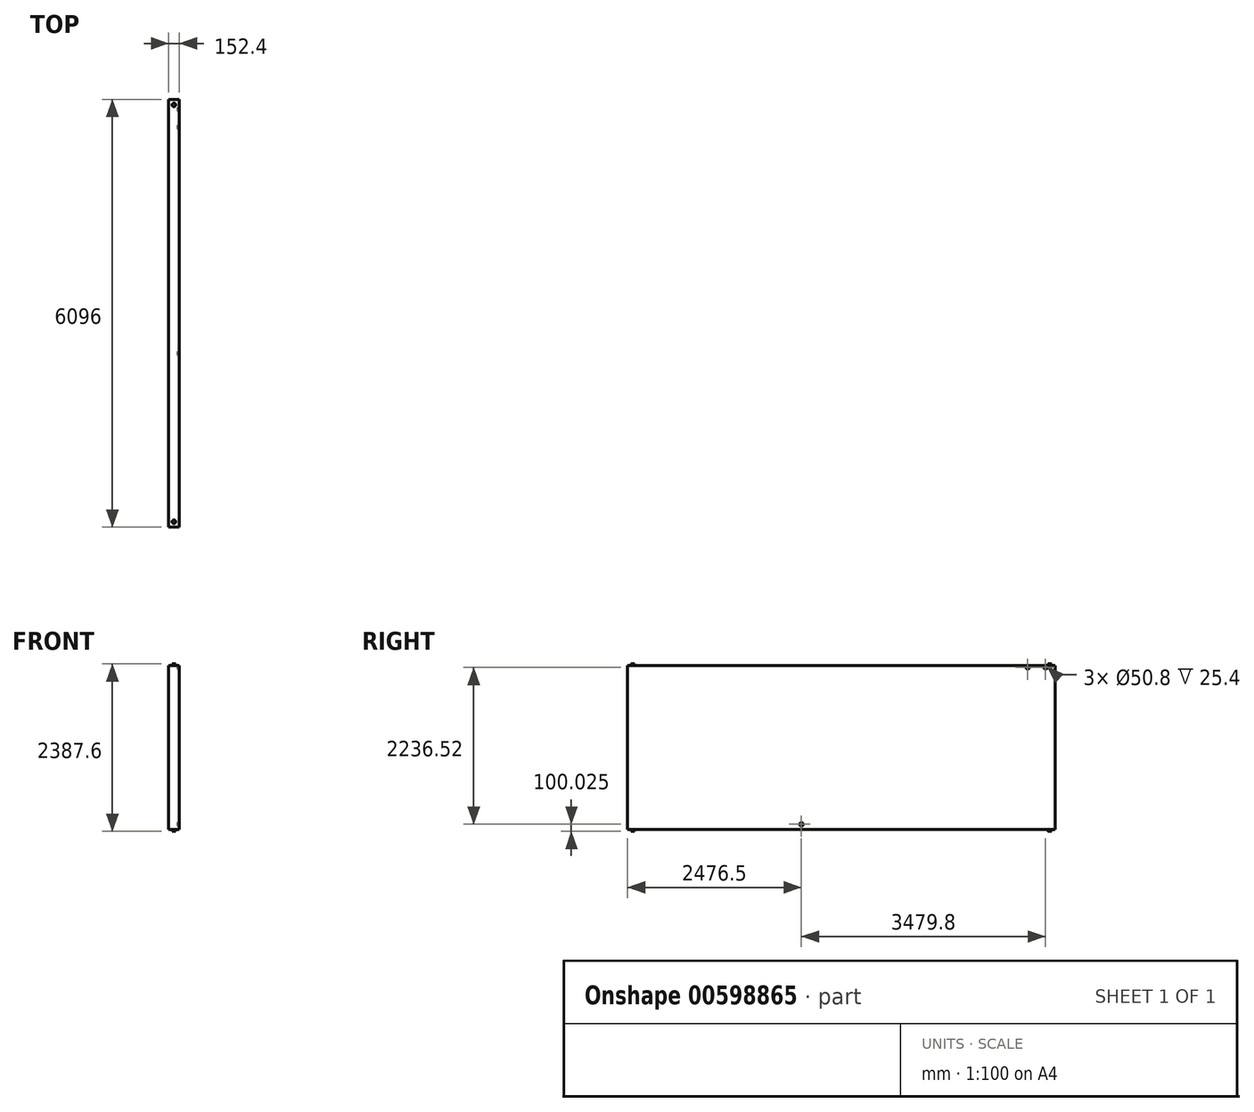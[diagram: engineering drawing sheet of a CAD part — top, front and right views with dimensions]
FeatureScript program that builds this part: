
annotation { "Feature Type Name" : "Feature", "Feature Type Description" : "" }
export const myFeature = defineFeature(function(context is Context, id is Id, definition is map)
    precondition{}
    {
        {
            var Q0;
            Q0=qCreatedBy(makeId("Top.planeOp"),FACE);
            var sketch = newSketch(context, id + "F0", { "sketchPlane" : qUnion([Q0])});
            skLineSegment(sketch, "E0.bottom", {"start": v(76.2, 3048) * mm, "end": v(-76.2, 3048) * mm});
            skLineSegment(sketch, "E0.top", {"start": v(76.2, -3048) * mm, "end": v(-76.2, -3048) * mm});
            skLineSegment(sketch, "E0.left", {"start": v(76.2, 3048) * mm, "end": v(76.2, -3048) * mm});
            skLineSegment(sketch, "E0.right", {"start": v(-76.2, 3048) * mm, "end": v(-76.2, -3048) * mm});
            skPoint(sketch, "E0.middle", {"position": v(0, 0) * mm});
            skSolve(sketch);
        }
        {
            var Q0;
            Q0=makeQuery(id+"F0.imprint","IMPRINT",FACE,{"disambiguationData":[TD([[makeQuery(id+"F0.imprint","IMPRINT",EDGE,{"derivedFrom":sQuery(id+"F0.wireOp",EDGE,"E0.bottom")}),1.0]])]});
            extrude(context, id + "F1", {"entities" : qUnion([Q0]), "depth" : 2336.8 * mm, "offsetDistance" : 25.4 * mm});
        }
        {
            var Q0;
            Q0=makeQuery(id+"F1.opExtrude","CAP_FACE",FACE,{"disambiguationData":[OSD([sQuery(id+"F0.wireOp",EDGE,"E0.bottom"),sQuery(id+"F0.wireOp",EDGE,"E0.top"),sQuery(id+"F0.wireOp",EDGE,"E0.left"),sQuery(id+"F0.wireOp",EDGE,"E0.right")])],"isStart":false});
            var sketch = newSketch(context, id + "F2", { "sketchPlane" : qUnion([Q0])});
            skLineSegment(sketch, "E1.bottom", {"start": v(76.2, -3048) * mm, "end": v(0, -3048) * mm});
            skLineSegment(sketch, "E1.top", {"start": v(76.2, -2971.8) * mm, "end": v(0, -2971.8) * mm});
            skLineSegment(sketch, "E1.left", {"start": v(76.2, -3048) * mm, "end": v(76.2, -2971.8) * mm});
            skLineSegment(sketch, "E1.right", {"start": v(0, -3048) * mm, "end": v(0, -2971.8) * mm});
            skCircle(sketch, "E2", {"center": v(0, -2971.8) * mm, "radius": 25.4 * mm});
            skLineSegment(sketch, "E3.bottom", {"start": v(76.2, 3048) * mm, "end": v(0, 3048) * mm});
            skLineSegment(sketch, "E3.top", {"start": v(76.2, 2971.8) * mm, "end": v(0, 2971.8) * mm});
            skLineSegment(sketch, "E3.left", {"start": v(76.2, 3048) * mm, "end": v(76.2, 2971.8) * mm});
            skLineSegment(sketch, "E3.right", {"start": v(0, 3048) * mm, "end": v(0, 2971.8) * mm});
            skCircle(sketch, "E4", {"center": v(0, 2971.8) * mm, "radius": 25.4 * mm});
            skSolve(sketch);
        }
        {
            var Q0;
            {var subQ0=sQuery(id+"F2.wireOp",EDGE,"E3.right");var subQ1=sQuery(id+"F2.wireOp",EDGE,"E3.top");var subQ2=makeQuery(id+"F2.imprint","INTERSECT",VERTEX,{"derivedFrom":[subQ1,subQ0]});Q0=makeQuery(id+"F2.imprint","IMPRINT",FACE,{"disambiguationData":[TD([[makeQuery(id+"F2.imprint","IMPRINT",EDGE,{"disambiguationData":[TD([[subQ2,1.0]])],"derivedFrom":subQ1}),-1.0]])]});}
            var Q1;
            {var subQ0=sQuery(id+"F2.wireOp",EDGE,"E3.right");var subQ1=sQuery(id+"F2.wireOp",EDGE,"E3.top");var subQ2=makeQuery(id+"F2.imprint","INTERSECT",VERTEX,{"derivedFrom":[subQ1,subQ0]});Q1=makeQuery(id+"F2.imprint","IMPRINT",FACE,{"disambiguationData":[TD([[makeQuery(id+"F2.imprint","IMPRINT",EDGE,{"disambiguationData":[TD([[subQ2,1.0]])],"derivedFrom":subQ1}),1.0]])]});}
            var Q2;
            {var subQ0=sQuery(id+"F2.wireOp",EDGE,"E1.right");var subQ1=sQuery(id+"F2.wireOp",EDGE,"E1.top");var subQ2=makeQuery(id+"F2.imprint","INTERSECT",VERTEX,{"derivedFrom":[subQ1,subQ0]});Q2=makeQuery(id+"F2.imprint","IMPRINT",FACE,{"disambiguationData":[TD([[makeQuery(id+"F2.imprint","IMPRINT",EDGE,{"disambiguationData":[TD([[subQ2,1.0]])],"derivedFrom":subQ1}),-1.0]])]});}
            var Q3;
            {var subQ0=sQuery(id+"F2.wireOp",EDGE,"E1.right");var subQ1=sQuery(id+"F2.wireOp",EDGE,"E1.top");var subQ2=makeQuery(id+"F2.imprint","INTERSECT",VERTEX,{"derivedFrom":[subQ1,subQ0]});Q3=makeQuery(id+"F2.imprint","IMPRINT",FACE,{"disambiguationData":[TD([[makeQuery(id+"F2.imprint","IMPRINT",EDGE,{"disambiguationData":[TD([[subQ2,1.0]])],"derivedFrom":subQ1}),1.0]])]});}
            extrude(context, id + "F3", {"entities" : qUnion([Q0, Q1, Q2, Q3]), "operationType" : NewBodyOperationType.ADD, "depth" : 25.4 * mm, "offsetDistance" : 25.4 * mm});
        }
        {
            var Q0;
            Q0=makeQuery(id+"F1.opExtrude","CAP_FACE",FACE,{"disambiguationData":[OSD([sQuery(id+"F0.wireOp",EDGE,"E0.bottom"),sQuery(id+"F0.wireOp",EDGE,"E0.top"),sQuery(id+"F0.wireOp",EDGE,"E0.left"),sQuery(id+"F0.wireOp",EDGE,"E0.right")])],"isStart":true});
            var sketch = newSketch(context, id + "F4", { "sketchPlane" : qUnion([Q0])});
            skLineSegment(sketch, "E5.bottom", {"start": v(76.2, 3048) * mm, "end": v(0, 3048) * mm});
            skLineSegment(sketch, "E5.top", {"start": v(76.2, 2971.8) * mm, "end": v(0, 2971.8) * mm});
            skLineSegment(sketch, "E5.left", {"start": v(76.2, 3048) * mm, "end": v(76.2, 2971.8) * mm});
            skLineSegment(sketch, "E5.right", {"start": v(0, 3048) * mm, "end": v(0, 2971.8) * mm});
            skCircle(sketch, "E6", {"center": v(0, 2971.8) * mm, "radius": 25.4 * mm});
            skLineSegment(sketch, "E7.bottom", {"start": v(76.2, -3048) * mm, "end": v(0, -3048) * mm});
            skLineSegment(sketch, "E7.top", {"start": v(76.2, -2971.8) * mm, "end": v(0, -2971.8) * mm});
            skLineSegment(sketch, "E7.left", {"start": v(76.2, -3048) * mm, "end": v(76.2, -2971.8) * mm});
            skLineSegment(sketch, "E7.right", {"start": v(0, -3048) * mm, "end": v(0, -2971.8) * mm});
            skCircle(sketch, "E8", {"center": v(0, -2971.8) * mm, "radius": 25.4 * mm});
            skSolve(sketch);
        }
        {
            var Q0;
            {var subQ0=sQuery(id+"F4.wireOp",EDGE,"E5.right");var subQ1=sQuery(id+"F4.wireOp",EDGE,"E5.top");var subQ2=makeQuery(id+"F4.imprint","INTERSECT",VERTEX,{"derivedFrom":[subQ1,subQ0]});Q0=makeQuery(id+"F4.imprint","IMPRINT",FACE,{"disambiguationData":[TD([[makeQuery(id+"F4.imprint","IMPRINT",EDGE,{"disambiguationData":[TD([[subQ2,1.0]])],"derivedFrom":subQ1}),-1.0]])]});}
            var Q1;
            {var subQ0=sQuery(id+"F4.wireOp",EDGE,"E5.right");var subQ1=sQuery(id+"F4.wireOp",EDGE,"E5.top");var subQ2=makeQuery(id+"F4.imprint","INTERSECT",VERTEX,{"derivedFrom":[subQ1,subQ0]});Q1=makeQuery(id+"F4.imprint","IMPRINT",FACE,{"disambiguationData":[TD([[makeQuery(id+"F4.imprint","IMPRINT",EDGE,{"disambiguationData":[TD([[subQ2,1.0]])],"derivedFrom":subQ1}),1.0]])]});}
            var Q2;
            {var subQ0=sQuery(id+"F4.wireOp",EDGE,"E7.right");var subQ1=sQuery(id+"F4.wireOp",EDGE,"E7.top");var subQ2=makeQuery(id+"F4.imprint","INTERSECT",VERTEX,{"derivedFrom":[subQ1,subQ0]});Q2=makeQuery(id+"F4.imprint","IMPRINT",FACE,{"disambiguationData":[TD([[makeQuery(id+"F4.imprint","IMPRINT",EDGE,{"disambiguationData":[TD([[subQ2,1.0]])],"derivedFrom":subQ1}),1.0]])]});}
            var Q3;
            {var subQ0=sQuery(id+"F4.wireOp",EDGE,"E7.right");var subQ1=sQuery(id+"F4.wireOp",EDGE,"E7.top");var subQ2=makeQuery(id+"F4.imprint","INTERSECT",VERTEX,{"derivedFrom":[subQ1,subQ0]});Q3=makeQuery(id+"F4.imprint","IMPRINT",FACE,{"disambiguationData":[TD([[makeQuery(id+"F4.imprint","IMPRINT",EDGE,{"disambiguationData":[TD([[subQ2,1.0]])],"derivedFrom":subQ1}),-1.0]])]});}
            extrude(context, id + "F5", {"entities" : qUnion([Q0, Q1, Q2, Q3]), "operationType" : NewBodyOperationType.ADD, "depth" : 25.4 * mm, "offsetDistance" : 25.4 * mm});
        }
        {
            var Q0;
            Q0=makeQuery(id+"F1.opExtrude","SWEPT_FACE",FACE,{"disambiguationData":[OSD([sQuery(id+"F0.wireOp",EDGE,"E0.left")])]});
            var sketch = newSketch(context, id + "F6", { "sketchPlane" : qUnion([Q0])});
            skCircle(sketch, "E9", {"center": v(2908.3, 2311.15) * mm, "radius": 25.4 * mm});
            skCircle(sketch, "E10", {"center": v(-571.5, 74.63) * mm, "radius": 25.4 * mm});
            skLineSegment(sketch, "E11.bottom", {"start": v(3048, 2336.8) * mm, "end": v(2908.3, 2336.8) * mm});
            skLineSegment(sketch, "E11.top", {"start": v(3048, 2311.15) * mm, "end": v(2908.3, 2311.15) * mm});
            skLineSegment(sketch, "E11.left", {"start": v(3048, 2336.8) * mm, "end": v(3048, 2311.15) * mm});
            skLineSegment(sketch, "E11.right", {"start": v(2908.3, 2336.8) * mm, "end": v(2908.3, 2311.15) * mm});
            skLineSegment(sketch, "E12", {"start": v(2908.3, 2311.15) * mm, "end": v(2654.3, 2311.15) * mm});
            skCircle(sketch, "E13", {"center": v(2654.3, 2311.15) * mm, "radius": 25.4 * mm});
            skLineSegment(sketch, "E14.bottom", {"start": v(-3048, 0) * mm, "end": v(-571.5, 0) * mm});
            skLineSegment(sketch, "E14.top", {"start": v(-3048, 74.63) * mm, "end": v(-571.5, 74.63) * mm});
            skLineSegment(sketch, "E14.left", {"start": v(-3048, 0) * mm, "end": v(-3048, 74.63) * mm});
            skLineSegment(sketch, "E14.right", {"start": v(-571.5, 0) * mm, "end": v(-571.5, 74.63) * mm});
            skSolve(sketch);
        }
        {
            var Q0;
            {var subQ0=sQuery(id+"F6.wireOp",EDGE,"E14.top");var subQ1=sQuery(id+"F6.wireOp",EDGE,"E10");var subQ2=makeQuery(id+"F6.imprint","INTERSECT",VERTEX,{"derivedFrom":[subQ1,subQ0]});Q0=makeQuery(id+"F6.imprint","IMPRINT",FACE,{"disambiguationData":[TD([[makeQuery(id+"F6.imprint","IMPRINT",EDGE,{"disambiguationData":[TD([[subQ2,1.0]])],"derivedFrom":subQ1}),1.0]])]});}
            var Q1;
            {var subQ0=sQuery(id+"F6.wireOp",EDGE,"E14.top");var subQ1=sQuery(id+"F6.wireOp",EDGE,"E10");var subQ2=makeQuery(id+"F6.imprint","INTERSECT",VERTEX,{"derivedFrom":[subQ1,subQ0]});Q1=makeQuery(id+"F6.imprint","IMPRINT",FACE,{"disambiguationData":[TD([[makeQuery(id+"F6.imprint","IMPRINT",EDGE,{"disambiguationData":[TD([[subQ2,-1.0]])],"derivedFrom":subQ1}),1.0]])]});}
            var Q2;
            {var subQ0=sQuery(id+"F6.wireOp",EDGE,"E11.right");var subQ1=sQuery(id+"F6.wireOp",EDGE,"E9");var subQ2=makeQuery(id+"F6.imprint","INTERSECT",VERTEX,{"derivedFrom":[subQ1,subQ0]});Q2=makeQuery(id+"F6.imprint","IMPRINT",FACE,{"disambiguationData":[TD([[makeQuery(id+"F6.imprint","IMPRINT",EDGE,{"disambiguationData":[TD([[subQ2,1.0]])],"derivedFrom":subQ1}),1.0]])]});}
            var Q3;
            {var subQ0=sQuery(id+"F6.wireOp",EDGE,"E12");var subQ1=sQuery(id+"F6.wireOp",EDGE,"E9");var subQ2=makeQuery(id+"F6.imprint","INTERSECT",VERTEX,{"derivedFrom":[subQ1,subQ0]});Q3=makeQuery(id+"F6.imprint","IMPRINT",FACE,{"disambiguationData":[TD([[makeQuery(id+"F6.imprint","IMPRINT",EDGE,{"disambiguationData":[TD([[subQ2,1.0]])],"derivedFrom":subQ1}),1.0]])]});}
            var Q4;
            {var subQ0=sQuery(id+"F6.wireOp",EDGE,"E12");var subQ1=sQuery(id+"F6.wireOp",EDGE,"E9");var subQ2=makeQuery(id+"F6.imprint","INTERSECT",VERTEX,{"derivedFrom":[subQ1,subQ0]});Q4=makeQuery(id+"F6.imprint","IMPRINT",FACE,{"disambiguationData":[TD([[makeQuery(id+"F6.imprint","IMPRINT",EDGE,{"disambiguationData":[TD([[subQ2,-1.0]])],"derivedFrom":subQ1}),1.0]])]});}
            var Q5;
            Q5=makeQuery(id+"F6.imprint","IMPRINT",FACE,{"disambiguationData":[TD([[makeQuery(id+"F6.imprint","IMPRINT",EDGE,{"derivedFrom":sQuery(id+"F6.wireOp",EDGE,"E13")}),1.0]])]});
            extrude(context, id + "F7", {"entities" : qUnion([Q0, Q1, Q2, Q3, Q4, Q5]), "operationType" : NewBodyOperationType.REMOVE, "oppositeDirection" : true, "depth" : 25.4 * mm, "offsetDistance" : 25.4 * mm});
        }
    });
